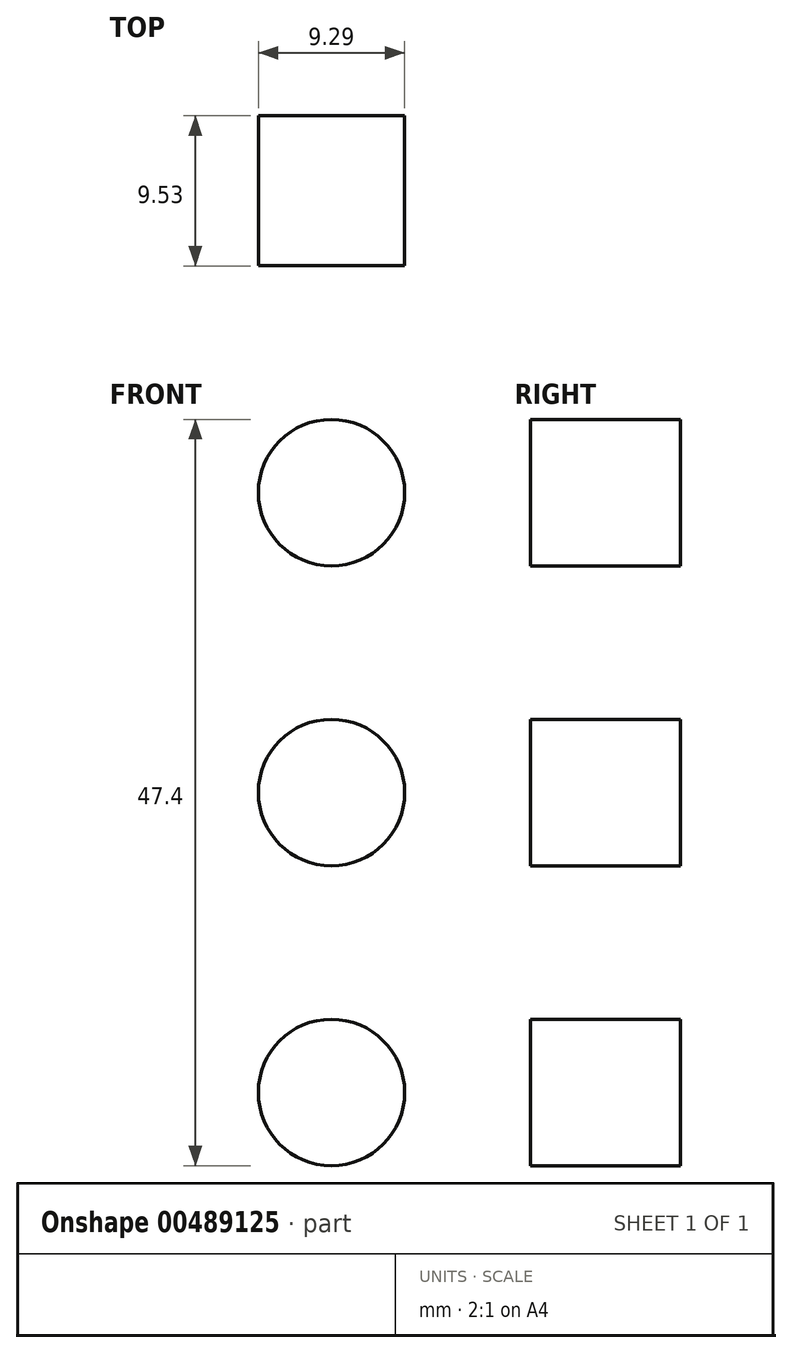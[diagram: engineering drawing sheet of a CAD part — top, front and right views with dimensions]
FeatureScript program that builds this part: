
annotation { "Feature Type Name" : "Feature", "Feature Type Description" : "" }
export const myFeature = defineFeature(function(context is Context, id is Id, definition is map)
    precondition{}
    {
        {
            var Q0;
            Q0=qCreatedBy(makeId("Front.planeOp"),FACE);
            var sketch = newSketch(context, id + "F0", { "sketchPlane" : qUnion([Q0])});
            skLineSegment(sketch, "E0", {"start": v(-160.02, 0) * mm, "end": v(160.02, 0) * mm});
            skLineSegment(sketch, "E1", {"start": v(-31.43, -64.77) * mm, "end": v(-106.52, -64.77) * mm});
            skLineSegment(sketch, "E2", {"start": v(-106.52, -64.77) * mm, "end": v(-106.52, -39.6) * mm});
            skLineSegment(sketch, "E3", {"start": v(-106.52, -39.6) * mm, "end": v(-167.95, -39.6) * mm});
            skLineSegment(sketch, "E4", {"start": v(-167.95, -39.6) * mm, "end": v(-167.95, 26.96) * mm});
            skLineSegment(sketch, "E5", {"start": v(0, 0) * mm, "end": v(0, 118.4) * mm, "construction": true});
            skLineSegment(sketch, "E6", {"start": v(0, 118.4) * mm, "end": v(0, -81.7) * mm, "construction": true});
            skLineSegment(sketch, "E7", {"start": v(0, -55.25) * mm, "end": v(-5.83, -55.25) * mm});
            skArc(sketch, "E8", {"start": v(-5.83, -55.25) * mm, "mid": v(-19.49, -57.7) * mm, "end": v(-31.43, -64.77) * mm});
            skFitSpline(sketch, "E9", {"points": [v(0, 104.31) * mm, v(-59.59, 99.2) * mm, v(-109.08, 87.67) * mm, v(-150.03, 66.77) * mm, v(-162.83, 48.85) * mm, v(-167.95, 26.96) * mm], "startDerivative": vector(-246.06, -15.43) * mm, "endDerivative": vector(0, -151.52) * mm});
            skFitSpline(sketch, "E10.MirrorCS", {"points": [v(0, 104.31) * mm, v(59.59, 99.2) * mm, v(109.08, 87.67) * mm, v(150.03, 66.77) * mm, v(162.83, 48.85) * mm, v(167.95, 26.96) * mm], "startDerivative": vector(246.06, -15.43) * mm, "endDerivative": vector(0, -151.52) * mm});
            skLineSegment(sketch, "E11.MirrorCS", {"start": v(167.95, -39.6) * mm, "end": v(167.95, 26.96) * mm});
            skLineSegment(sketch, "E12.MirrorCS", {"start": v(106.52, -39.6) * mm, "end": v(167.95, -39.6) * mm});
            skLineSegment(sketch, "E13.MirrorCS", {"start": v(106.52, -64.77) * mm, "end": v(106.52, -39.6) * mm});
            skLineSegment(sketch, "E14.MirrorCS", {"start": v(31.43, -64.77) * mm, "end": v(106.52, -64.77) * mm});
            skArc(sketch, "E15.MirrorCS", {"start": v(5.83, -55.25) * mm, "mid": v(19.49, -57.7) * mm, "end": v(31.43, -64.77) * mm});
            skLineSegment(sketch, "E16.MirrorCS", {"start": v(0, -55.25) * mm, "end": v(5.83, -55.25) * mm});
            skCircle(sketch, "E17", {"center": v(-96.87, -55.63) * mm, "radius": 6.35 * mm});
            skCircle(sketch, "E18", {"center": v(-75.53, -55.63) * mm, "radius": 6.35 * mm});
            skCircle(sketch, "E19", {"center": v(75.53, -55.63) * mm, "radius": 6.35 * mm});
            skCircle(sketch, "E20", {"center": v(96.87, -55.63) * mm, "radius": 6.35 * mm});
            skCircle(sketch, "E21", {"center": v(150.17, 53.62) * mm, "radius": 6.35 * mm});
            skCircle(sketch, "E22", {"center": v(-150.17, 53.62) * mm, "radius": 6.35 * mm});
            skSolve(sketch);
        }
        {
            var Q0;
            Q0=makeQuery(id+"F0.imprint","IMPRINT",FACE,{"disambiguationData":[TD([[makeQuery(id+"F0.imprint","IMPRINT",EDGE,{"derivedFrom":sQuery(id+"F0.wireOp",EDGE,"E1")}),-1.0]])]});
            extrude(context, id + "F1", {"entities" : qUnion([Q0]), "depth" : 9.52 * mm});
        }
        {
            var Q0;
            Q0=makeQuery(id+"F1.opExtrude","SWEPT_EDGE",EDGE,{"disambiguationData":[OSD([sQuery(id+"F0.wireOp",EDGE,"E11.MirrorCS"),sQuery(id+"F0.wireOp",EDGE,"E12.MirrorCS")])]});
            var Q1;
            Q1=makeQuery(id+"F1.opExtrude","SWEPT_EDGE",EDGE,{"disambiguationData":[OSD([sQuery(id+"F0.wireOp",EDGE,"E3"),sQuery(id+"F0.wireOp",EDGE,"E4")])]});
            fillet(context, id + "F2", {"entities" : qUnion([Q0, Q1]), "radius" : 10.16 * mm, "tangentPropagation" : true, "allowEdgeOverflow" : false});
        }
        {
            var Q0;
            Q0=makeQuery(id+"F1.opExtrude","CAP_FACE",FACE,{"disambiguationData":[OSD([sQuery(id+"F0.wireOp",EDGE,"E1"),sQuery(id+"F0.wireOp",EDGE,"E2"),sQuery(id+"F0.wireOp",EDGE,"E3"),sQuery(id+"F0.wireOp",EDGE,"E4"),sQuery(id+"F0.wireOp",EDGE,"E7"),sQuery(id+"F0.wireOp",EDGE,"E8"),sQuery(id+"F0.wireOp",EDGE,"E9"),sQuery(id+"F0.wireOp",EDGE,"E10.MirrorCS"),sQuery(id+"F0.wireOp",EDGE,"E11.MirrorCS"),sQuery(id+"F0.wireOp",EDGE,"E12.MirrorCS"),sQuery(id+"F0.wireOp",EDGE,"E13.MirrorCS"),sQuery(id+"F0.wireOp",EDGE,"E14.MirrorCS"),sQuery(id+"F0.wireOp",EDGE,"E15.MirrorCS"),sQuery(id+"F0.wireOp",EDGE,"E16.MirrorCS"),sQuery(id+"F0.wireOp",EDGE,"E17"),sQuery(id+"F0.wireOp",EDGE,"E18"),sQuery(id+"F0.wireOp",EDGE,"E19"),sQuery(id+"F0.wireOp",EDGE,"E20"),sQuery(id+"F0.wireOp",EDGE,"E21"),sQuery(id+"F0.wireOp",EDGE,"E22")])],"isStart":false});
            var sketch = newSketch(context, id + "F3", { "sketchPlane" : qUnion([Q0])});
            skLineSegment(sketch, "E23.bottom", {"start": v(-89.48, 80.09) * mm, "end": v(89.48, 80.09) * mm, "construction": true});
            skLineSegment(sketch, "E23.top", {"start": v(-89.48, -30.7) * mm, "end": v(89.48, -30.7) * mm, "construction": true});
            skLineSegment(sketch, "E23.left", {"start": v(-96.5, 73.08) * mm, "end": v(-96.5, -23.7) * mm, "construction": true});
            skLineSegment(sketch, "E23.right", {"start": v(96.5, 73.08) * mm, "end": v(96.5, -23.7) * mm, "construction": true});
            skPoint(sketch, "E24.visualSharp", {"position": v(-96.5, 80.09) * mm});
            skArc(sketch, "E24.filletArc", {"start": v(-89.48, 80.09) * mm, "mid": v(-94.44, 78.03) * mm, "end": v(-96.5, 73.08) * mm, "construction": true});
            skPoint(sketch, "E25.visualSharp", {"position": v(-96.5, -30.7) * mm});
            skArc(sketch, "E25.filletArc", {"start": v(-96.5, -23.7) * mm, "mid": v(-94.44, -28.66) * mm, "end": v(-89.48, -30.7) * mm, "construction": true});
            skPoint(sketch, "E26.visualSharp", {"position": v(96.5, -30.7) * mm});
            skArc(sketch, "E26.filletArc", {"start": v(89.48, -30.7) * mm, "mid": v(94.44, -28.66) * mm, "end": v(96.5, -23.7) * mm, "construction": true});
            skPoint(sketch, "E27.visualSharp", {"position": v(96.5, 80.09) * mm});
            skArc(sketch, "E27.filletArc", {"start": v(96.5, 73.08) * mm, "mid": v(94.44, 78.03) * mm, "end": v(89.48, 80.09) * mm, "construction": true});
            skLineSegment(sketch, "E28.0", {"start": v(-89.48, -31.47) * mm, "end": v(89.48, -31.47) * mm});
            skLineSegment(sketch, "E28.1", {"start": v(-89.48, 80.85) * mm, "end": v(89.48, 80.85) * mm});
            skArc(sketch, "E28.2", {"start": v(97.26, 73.08) * mm, "mid": v(94.98, 78.57) * mm, "end": v(89.48, 80.85) * mm});
            skLineSegment(sketch, "E28.3", {"start": v(97.26, 73.08) * mm, "end": v(97.26, -23.7) * mm});
            skArc(sketch, "E28.4", {"start": v(89.48, -31.47) * mm, "mid": v(94.98, -29.2) * mm, "end": v(97.26, -23.7) * mm});
            skArc(sketch, "E29.0", {"start": v(-97.26, -23.7) * mm, "mid": v(-94.98, -29.2) * mm, "end": v(-89.48, -31.47) * mm});
            skLineSegment(sketch, "E29.1", {"start": v(-97.26, 73.08) * mm, "end": v(-97.26, -23.7) * mm});
            skArc(sketch, "E29.2", {"start": v(-89.48, 80.85) * mm, "mid": v(-94.98, 78.57) * mm, "end": v(-97.26, 73.08) * mm});
            skSolve(sketch);
        }
        {
            var Q0;
            Q0=makeQuery(id+"F3.imprint","IMPRINT",FACE,{"disambiguationData":[TD([[makeQuery(id+"F3.imprint","IMPRINT",EDGE,{"derivedFrom":sQuery(id+"F3.wireOp",EDGE,"E28.0")}),1.0]])]});
            extrude(context, id + "F4", {"entities" : qUnion([Q0]), "operationType" : NewBodyOperationType.REMOVE, "oppositeDirection" : true, "depth" : 25.4 * mm});
        }
        {
            var Q0;
            Q0=makeQuery(id+"F1.opExtrude","SWEPT_EDGE",EDGE,{"disambiguationData":[OSD([sQuery(id+"F0.wireOp",EDGE,"E9"),sQuery(id+"F0.wireOp",EDGE,"E10.MirrorCS")])]});
            fillet(context, id + "F5", {"entities" : qUnion([Q0]), "radius" : 254 * mm, "tangentPropagation" : true, "allowEdgeOverflow" : false});
        }
        {
            var Q0;
            Q0=makeQuery(id+"F1.opExtrude","CAP_FACE",FACE,{"disambiguationData":[OSD([sQuery(id+"F0.wireOp",EDGE,"E1"),sQuery(id+"F0.wireOp",EDGE,"E2"),sQuery(id+"F0.wireOp",EDGE,"E3"),sQuery(id+"F0.wireOp",EDGE,"E4"),sQuery(id+"F0.wireOp",EDGE,"E7"),sQuery(id+"F0.wireOp",EDGE,"E8"),sQuery(id+"F0.wireOp",EDGE,"E9"),sQuery(id+"F0.wireOp",EDGE,"E10.MirrorCS"),sQuery(id+"F0.wireOp",EDGE,"E11.MirrorCS"),sQuery(id+"F0.wireOp",EDGE,"E12.MirrorCS"),sQuery(id+"F0.wireOp",EDGE,"E13.MirrorCS"),sQuery(id+"F0.wireOp",EDGE,"E14.MirrorCS"),sQuery(id+"F0.wireOp",EDGE,"E15.MirrorCS"),sQuery(id+"F0.wireOp",EDGE,"E16.MirrorCS"),sQuery(id+"F0.wireOp",EDGE,"E17"),sQuery(id+"F0.wireOp",EDGE,"E18"),sQuery(id+"F0.wireOp",EDGE,"E19"),sQuery(id+"F0.wireOp",EDGE,"E20"),sQuery(id+"F0.wireOp",EDGE,"E21"),sQuery(id+"F0.wireOp",EDGE,"E22")])],"isStart":false});
            var sketch = newSketch(context, id + "F6", { "sketchPlane" : qUnion([Q0])});
            skCircle(sketch, "E30", {"center": v(-134.93, 1.04) * mm, "radius": 14.16 * mm});
            skCircle(sketch, "E31", {"center": v(134.93, 1.04) * mm, "radius": 14.16 * mm});
            skCircle(sketch, "E32", {"center": v(110.58, 31.09) * mm, "radius": 4.65 * mm});
            skCircle(sketch, "E33", {"center": v(110.58, 12.04) * mm, "radius": 4.65 * mm});
            skCircle(sketch, "E34", {"center": v(110.58, -7.01) * mm, "radius": 4.65 * mm});
            skLineSegment(sketch, "E35", {"start": v(110.58, -5.57) * mm, "end": v(110.58, 75.14) * mm, "construction": true});
            skLineSegment(sketch, "E36", {"start": v(0, 0) * mm, "end": v(0, 110.57) * mm, "construction": true});
            skPoint(sketch, "E36.endSnap0", {"position": v(0, 80.85) * mm});
            skCircle(sketch, "E37", {"center": v(132.85, 31.09) * mm, "radius": 4.65 * mm});
            skCircle(sketch, "E38.MirrorC", {"center": v(-110.58, 31.09) * mm, "radius": 4.65 * mm});
            skCircle(sketch, "E39.MirrorC", {"center": v(-110.58, 12.04) * mm, "radius": 4.65 * mm});
            skCircle(sketch, "E40.MirrorC", {"center": v(-110.58, -7.01) * mm, "radius": 4.65 * mm});
            skLineSegment(sketch, "E41", {"start": v(110.58, 31.09) * mm, "end": v(132.85, 31.09) * mm, "construction": true});
            skSolve(sketch);
        }
        {
            var Q0;
            Q0=makeQuery(id+"F6.imprint","IMPRINT",FACE,{"disambiguationData":[TD([[makeQuery(id+"F6.imprint","IMPRINT",EDGE,{"derivedFrom":sQuery(id+"F6.wireOp",EDGE,"E39.MirrorC")}),-1.0]])]});
            var Q1;
            Q1=makeQuery(id+"F6.imprint","IMPRINT",FACE,{"disambiguationData":[TD([[makeQuery(id+"F6.imprint","IMPRINT",EDGE,{"derivedFrom":sQuery(id+"F6.wireOp",EDGE,"E38.MirrorC")}),-1.0]])]});
            var Q2;
            Q2=makeQuery(id+"F6.imprint","IMPRINT",FACE,{"disambiguationData":[TD([[makeQuery(id+"F6.imprint","IMPRINT",EDGE,{"derivedFrom":sQuery(id+"F6.wireOp",EDGE,"E40.MirrorC")}),-1.0]])]});
            var Q3;
            Q3=makeQuery(id+"F6.imprint","IMPRINT",FACE,{"disambiguationData":[TD([[makeQuery(id+"F6.imprint","IMPRINT",EDGE,{"derivedFrom":sQuery(id+"F6.wireOp",EDGE,"E30")}),1.0]])]});
            var Q4;
            Q4=makeQuery(id+"F6.imprint","IMPRINT",FACE,{"disambiguationData":[TD([[makeQuery(id+"F6.imprint","IMPRINT",EDGE,{"derivedFrom":sQuery(id+"F6.wireOp",EDGE,"E32")}),1.0]])]});
            var Q5;
            Q5=makeQuery(id+"F6.imprint","IMPRINT",FACE,{"disambiguationData":[TD([[makeQuery(id+"F6.imprint","IMPRINT",EDGE,{"derivedFrom":sQuery(id+"F6.wireOp",EDGE,"E33")}),1.0]])]});
            var Q6;
            Q6=makeQuery(id+"F6.imprint","IMPRINT",FACE,{"disambiguationData":[TD([[makeQuery(id+"F6.imprint","IMPRINT",EDGE,{"derivedFrom":sQuery(id+"F6.wireOp",EDGE,"E34")}),1.0]])]});
            var Q7;
            Q7=makeQuery(id+"F6.imprint","IMPRINT",FACE,{"disambiguationData":[TD([[makeQuery(id+"F6.imprint","IMPRINT",EDGE,{"derivedFrom":sQuery(id+"F6.wireOp",EDGE,"E37")}),1.0]])]});
            var Q8;
            Q8=makeQuery(id+"F6.imprint","IMPRINT",FACE,{"disambiguationData":[TD([[makeQuery(id+"F6.imprint","IMPRINT",EDGE,{"derivedFrom":sQuery(id+"F6.wireOp",EDGE,"E31")}),1.0]])]});
            extrude(context, id + "F7", {"entities" : qUnion([Q0, Q1, Q2, Q3, Q4, Q5, Q6, Q7, Q8]), "operationType" : NewBodyOperationType.REMOVE, "oppositeDirection" : true, "depth" : 25.4 * mm});
        }
    });
